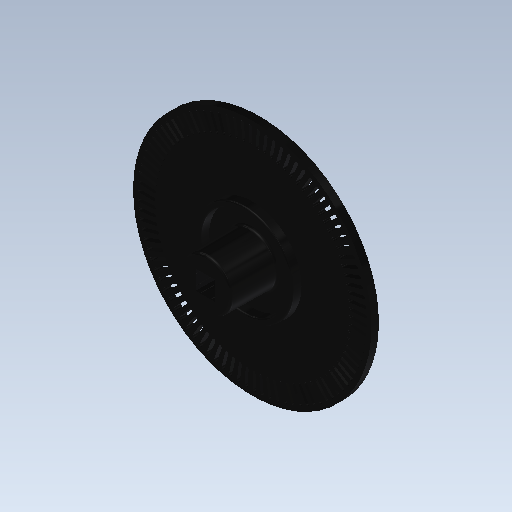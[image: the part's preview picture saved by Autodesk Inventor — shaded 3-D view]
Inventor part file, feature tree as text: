
AUTODESK INVENTOR PART (.ipt)
format: ipt  version: 2020 (Build 240168000, 168)  size: 538,112 bytes
history: native  units: in
note: dims shown in document units (in); Inventor stores cm internally (conversion verified against a paired STEP export)
features: extrude x6, sketch x6, fillet x2, mirror x1, pattern_circular x1, other x1
ambient origin geometry x8: Origin, YZ Plane, XZ Plane, XY Plane, X Axis, Y Axis, Z Axis, Center Point
bodies: Solid1 (feature_tree)
feature tree (17):
  extrude  "Extrusion1"  Depth=0.049in TaperAngle=0.0deg
  extrude  "Extrusion2"  Depth=0.31in
  fillet  "Fillet1"  Radius=0.02in
  extrude  "Extrusion3"  Depth=0.059in
  fillet  "Fillet2"  Radius=0.059in
  mirror  "Mirror1"
  extrude  "Extrusion4"  Depth=0.059in TaperAngle=0.0deg
  extrude  "Extrusion5"  Depth=0.059in TaperAngle=360.0deg
  pattern_circular  "Circular Pattern1"  [2 undecoded]
  sketch  "Sketch1"  dims[d0=1.575in d1=0.049in d2=0.0in]
  sketch  "Sketch2"  dims[d3=0.3401in d4=0.31in d5=-0.0034in d6=0.02in]
  sketch  "Sketch3"  dims[d7=0.5688in d8=0.041in d9=0.059in d10=-0.0069in]
  sketch  "Sketch4"  dims[d11=0.012in d12=0.059in d13=0.0in]
  sketch  "Sketch5"  dims[d14=0.059in d15=0.0in d16=35.4331in d17=360.0deg]
  sketch  "Sketch6"  dims[d19=0.059in d20=0.0in d21=0.0in d22=0.0in]
  other  "Srf1"
  extrude  "ExtrusionSrf1"  TaperAngle=0.0deg  [1 undecoded]
note: 3 required parameter values undecoded (feature->parameter linkage not recoverable at this tier; creation-order binding heuristic only, values carry confidence <= 0.55)
